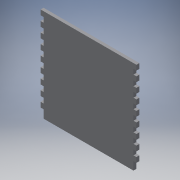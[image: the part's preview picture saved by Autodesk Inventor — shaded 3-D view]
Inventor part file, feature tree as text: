
AUTODESK INVENTOR PART (.ipt)
format: ipt  version: 2019 (Build 230136000, 136)  size: 226,304 bytes
history: native  units: mm
features: reference x20, other x5, extrude x2, sketch x2, projected_geometry x1
ambient origin geometry x8: Origin, YZ Plane, XZ Plane, XY Plane, X Axis, Y Axis, Z Axis, Center Point
bodies: Body1 (feature_tree)
feature tree (30):
  other  "Твердое тело1"
  extrude  "Выдавливание1"  Depth=6.0mm TaperAngle=0.0deg
  extrude  "Выдавливание2"  Depth=15.0mm
  sketch  "Эскиз1"
  reference  "Ссылка1"
  reference  "Ссылка2"
  reference  "Ссылка3"
  reference  "Ссылка4"
  reference  "Ссылка5"
  reference  "Ссылка6"
  reference  "Ссылка7"
  reference  "Ссылка8"
  reference  "Ссылка9"
  reference  "Ссылка10"
  reference  "Ссылка11"
  reference  "Ссылка12"
  reference  "Ссылка13"
  reference  "Ссылка14"
  reference  "Ссылка15"
  reference  "Ссылка16"
  reference  "Ссылка17"
  reference  "Ссылка18"
  reference  "Ссылка19"
  reference  "Ссылка20"
  sketch  "Эскиз2"
  projected_geometry  "Спроецированная петля1"
  other  "<userpath>\Desktop\Новая папка (7)\Сборка2.iam"
  other  "Сборка2.iam"
  other  "боковина:1"
  other  "боковина:2"
